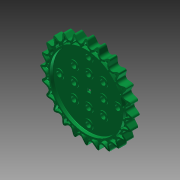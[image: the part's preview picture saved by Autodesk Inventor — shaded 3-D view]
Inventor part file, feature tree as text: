
AUTODESK INVENTOR PART (.ipt)
format: ipt  version: 2014 SP1 (Build 180222100, 222)  size: 3,453,440 bytes
history: native  units: in
note: dims shown in document units (in); Inventor stores cm internally (conversion verified against a paired STEP export)
features: extrude x2, sketch x2, other x1, imported_body x1
ambient origin geometry x8: Origin, YZ Plane, XZ Plane, XY Plane, X Axis, Y Axis, Z Axis, Center Point
bodies: Body1 (feature_tree)
feature tree (6):
  parser-record x1  (decoder bookkeeping rows leaked as tree rows — omitted from the tree; the rows remain in map.json)
  imported_body  "Base1"
  extrude  "Extrusion1"  Depth=1.0in TaperAngle=0.0deg
  extrude  "Extrusion2"  [1 undecoded]
  sketch  "Sketch1"  dims[d0=1.0in d1=0.0in d2=1.0in d3=0.0in]
  sketch  "Sketch2"
note: 1 required parameter value undecoded (feature->parameter linkage not recoverable at this tier; creation-order binding heuristic only, values carry confidence <= 0.55)
